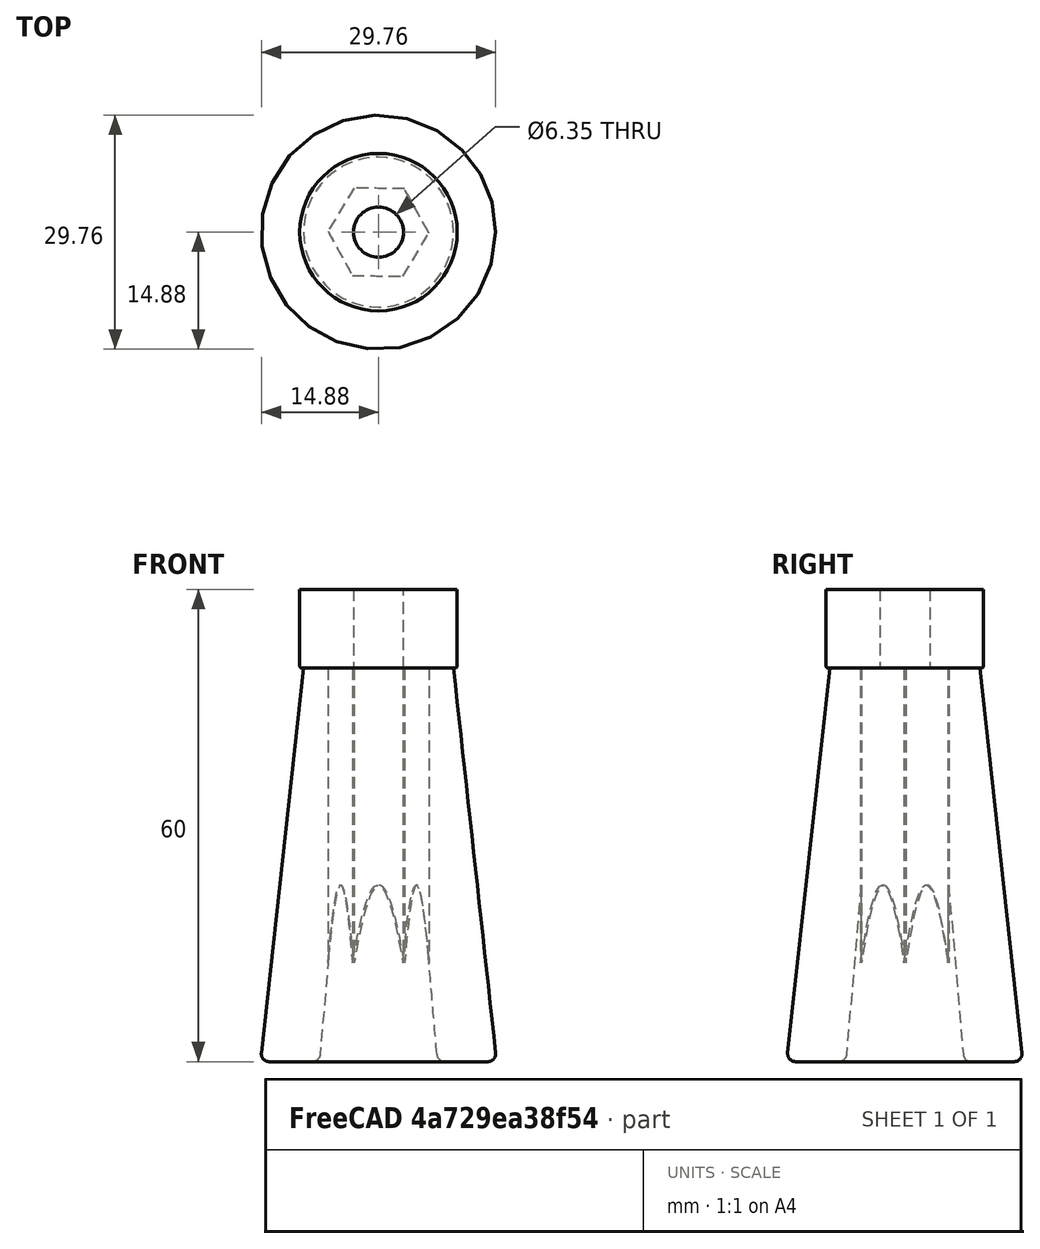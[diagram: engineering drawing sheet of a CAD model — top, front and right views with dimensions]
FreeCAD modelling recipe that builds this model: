
FCSTD DOCUMENT  (FreeCAD 0.19R24291 (Git))
Label: WorkBenchHandle_0_25x20Bolt
License: All rights reserved
LicenseURL: http://en.wikipedia.org/wiki/All_rights_reserved
objects: TechDraw::DrawViewDimension×9, Sketcher::SketchObject×5, TechDraw::DrawProjGroupItem×4, PartDesign::Pocket×2, PartDesign::Fillet×2, PartDesign::AdditiveLoft×1, PartDesign::Pad×1, TechDraw::DrawSVGTemplate×1, PartDesign::Body×1, TechDraw::DrawProjGroup×1, TechDraw::DrawPage×1
note: 18 computed .brp shape members not serialized (recipe doc carries the construction recipe); baked Part::Feature solids carry a one-line shape summary decoded from their .brp

FEATURE [Sketcher::SketchObject] Sketch
  FullyConstrained = true
  MapMode = 5
  Support = -> [XY_Plane]
  sketch-geometry (2):
    g0: Circle CenterX=0 CenterY=0 CenterZ=0 NormalX=0 NormalY=0 NormalZ=1 AngleXU=0 Radius=15
    g1: Circle CenterX=0 CenterY=0 CenterZ=0 NormalX=0 NormalY=0 NormalZ=1 AngleXU=0 Radius=7.5
  constraints (4):
    c: Coincident(g0,g-1)
    c: Coincident(g1,g0)
    c: Diameter(g0) = 30
    c: Diameter(g1) = 15
FEATURE [Sketcher::SketchObject] Sketch001
  AttachmentOffset = pos=(0,0,50) rot=(0,0,1;0rad)
  FullyConstrained = true
  MapMode = 5
  Placement = pos=(0,0,50) rot=(0,0,1;0rad)
  Support = -> [XY_Plane]
  sketch-geometry (2):
    g0: Circle CenterX=0 CenterY=0 CenterZ=0 NormalX=0 NormalY=0 NormalZ=1 AngleXU=0 Radius=9.525
    g1: Circle CenterX=0 CenterY=0 CenterZ=0 NormalX=0 NormalY=0 NormalZ=1 AngleXU=0 Radius=3.175
  constraints (4):
    c: Coincident(g0,g-1)
    c: Coincident(g1,g0)
    c: Diameter(g0) = 19.05
    c: Diameter(g1) = 6.35
FEATURE [PartDesign::AdditiveLoft] AdditiveLoft  label="AdditiveLoftHandel"
  Closed = false
  Profile = -> Sketch
  Ruled = false
  Sections = -> [Sketch001]
FEATURE [Sketcher::SketchObject] Sketch002
  FullyConstrained = true
  MapMode = 5
  Placement = pos=(0,0,50) rot=(0,0,1;0rad)
  Support = -> [AdditiveLoft]
  sketch-geometry (1):
    g0: Circle CenterX=0 CenterY=0 CenterZ=0 NormalX=0 NormalY=0 NormalZ=1 AngleXU=0 Radius=10
  constraints (2):
    c: Coincident(g0,g-1)
    c: Diameter(g0) = 20
FEATURE [PartDesign::Pad] Pad  label="PadBoss"
  BaseFeature = -> AdditiveLoft
  Direction = (1,1,1)
  Length = 10
  Length2 = 100
  Profile = -> Sketch002
  Type = 0
FEATURE [TechDraw::DrawSVGTemplate] Template
  EditableTexts = Approved1=Approved 1; Approved2=Approved 2; CheckedBy=on 20230706; Code=Code; CompanyAddress=3433 Riegeway Trail; CompanyName=Amused Scientist; DrawingNumber=Drawing Number; DrawingTitle1=WorkBenchHandle; DrawingTitle2=Drawing Title 2; DrawingTitle3=Drawing Title 3; DrawnBy=Lee Erickson; Revision=Rev; Scale=Scale 1:1; Sheet=Sheet n of m
  Height = 215.9
  Orientation = 1
  Width = 279.4
FEATURE [Sketcher::SketchObject] Sketch003
  FullyConstrained = true
  MapMode = 5
  Support = -> [XY_Plane]
  sketch-geometry (1):
    g0: Circle CenterX=0 CenterY=0 CenterZ=0 NormalX=0 NormalY=0 NormalZ=1 AngleXU=0 Radius=3.175
  constraints (2):
    c: Coincident(g0,g-1)
    c: Diameter(g0) = 6.35
FEATURE [PartDesign::Pocket] Pocket  label="PocketBoltHole"
  BaseFeature = -> Pad
  Length = 5.08
  Length2 = 100.076
  Profile = -> Sketch003
  Reversed = true
  Type = 1
FEATURE [Sketcher::SketchObject] Sketch004
  FullyConstrained = false
  MapMode = 5
  Placement = pos=(0,0,50) rot=(0,0,1;0rad)
  Support = -> [AdditiveLoft]
  sketch-geometry (7):
    g0: LineSegment StartX=6.41484 StartY=-0.111105 StartZ=0 EndX=3.30364 EndY=5.49986 EndZ=0
    g1: LineSegment StartX=3.30364 StartY=5.49986 StartZ=0 EndX=-3.1112 EndY=5.61097 EndZ=0
    g2: LineSegment StartX=-3.1112 StartY=5.61097 StartZ=0 EndX=-6.41484 EndY=0.111105 EndZ=0
    g3: LineSegment StartX=-6.41484 StartY=0.111105 StartZ=0 EndX=-3.30364 EndY=-5.49986 EndZ=0
    g4: LineSegment StartX=-3.30364 StartY=-5.49986 StartZ=0 EndX=3.1112 EndY=-5.61097 EndZ=0
    g5: LineSegment StartX=3.1112 StartY=-5.61097 StartZ=0 EndX=6.41484 EndY=-0.111105 EndZ=0
    g6: Circle CenterX=0 CenterY=0 CenterZ=0 NormalX=0 NormalY=0 NormalZ=1 AngleXU=0 Radius=6.4158
  constraints (15):
    c: Coincident(g0,g1)
    c: Coincident(g1,g2)
    c: Coincident(g2,g3)
    c: Coincident(g3,g4)
    c: Coincident(g4,g5)
    c: Coincident(g5,g0)
    c: Equal(g0, g1-g5) x5
    c: PointOnObject(g0,g6)
    c: PointOnObject(g1,g6)
    c: PointOnObject(g2,g6)
    c: PointOnObject(g3,g6)
    c: PointOnObject(g4,g6)
    c: PointOnObject(g5,g6)
    c: Coincident(g6,g-1)
    c: Distance(g1,g0) = 11.1125
FEATURE [PartDesign::Pocket] Pocket001
  BaseFeature = -> Pocket
  Length = 5.08
  Length2 = 100.076
  Profile = -> Sketch004
  Type = 1
FEATURE [PartDesign::Fillet] Fillet
  Base = -> Pocket001 [Edge2]
  BaseFeature = -> Pocket001
  Radius = 0.254
  SupportTransform = false
FEATURE [PartDesign::Fillet] Fillet001
  Base = -> Fillet [Edge18,Edge10]
  BaseFeature = -> Fillet
  Radius = 0.999998
  SupportTransform = false
FEATURE [PartDesign::Body] Body
  Group = -> [Sketch,Sketch001,AdditiveLoft,Sketch002,Pad,Sketch003,Pocket,Sketch004,Pocket001,Fillet,Fillet001]
  Origin = -> Origin
  Tip = -> Fillet001
FEATURE [TechDraw::DrawProjGroupItem] ProjItem004  label="Front001"
  CoarseView = false
  Direction = (1,0,0)
  Focus = 100
  HardHidden = false
  IsoCount = 0
  IsoHidden = false
  IsoVisible = false
  LockPosition = true
  Perspective = false
  Rotation = 0
  RotationVector = (0,0,1)
  ScaleType = 2
  SeamHidden = false
  SeamVisible = false
  SmoothHidden = false
  SmoothVisible = false
  Source = -> [Body]
  Type = 0
  X = 0
  XDirection = (0,0,1)
  Y = 0
FEATURE [TechDraw::DrawProjGroupItem] ProjItem005  label="FrontBottomLeft001"
  CoarseView = false
  Direction = (0.57735,0.57735,-0.57735)
  Focus = 100
  HardHidden = false
  IsoCount = 0
  IsoHidden = false
  IsoVisible = false
  LockPosition = true
  Perspective = false
  Rotation = 0
  RotationVector = (1,0,0)
  ScaleType = 2
  SeamHidden = false
  SeamVisible = false
  SmoothHidden = false
  SmoothVisible = false
  Source = -> [Body]
  Type = 8
  X = 90.1975
  XDirection = (0.707107,0,0.707107)
  Y = 67.4708
FEATURE [TechDraw::DrawProjGroupItem] ProjItem006  label="Right001"
  CoarseView = false
  Direction = (1e-16,0,1)
  Focus = 100
  HardHidden = false
  IsoCount = 0
  IsoHidden = false
  IsoVisible = false
  LockPosition = true
  Perspective = false
  Rotation = 0
  RotationVector = (1,0,0)
  ScaleType = 2
  SeamHidden = false
  SeamVisible = false
  SmoothHidden = false
  SmoothVisible = false
  Source = -> [Body]
  Type = 2
  X = -69.895
  XDirection = (-1,0,1e-16)
  Y = 0
FEATURE [TechDraw::DrawProjGroupItem] ProjItem007  label="FrontBottomRight001"
  CoarseView = false
  Direction = (0.57735,0.57735,0.57735)
  Focus = 100
  HardHidden = false
  IsoCount = 0
  IsoHidden = false
  IsoVisible = false
  LockPosition = true
  Perspective = false
  Rotation = 0
  RotationVector = (1,0,0)
  ScaleType = 2
  SeamHidden = false
  SeamVisible = false
  SmoothHidden = false
  SmoothVisible = false
  Source = -> [Body]
  Type = 9
  X = -5.79715
  XDirection = (-0.707107,0,0.707107)
  Y = 61.3243
FEATURE [TechDraw::DrawProjGroup] ProjGroup001  label="ProjGroup"
  Anchor = -> ProjItem004
  AutoDistribute = true
  LockPosition = false
  ProjectionType = 0
  Rotation = 0
  ScaleType = 0
  Source = -> [Body]
  Views = -> [ProjItem004,ProjItem005,ProjItem006,ProjItem007]
  X = 120.351
  Y = 96.2835
  spacingX = 15
  spacingY = 15
FEATURE [TechDraw::DrawViewDimension] Dimension010
  Arbitrary = false
  ArbitraryTolerances = false
  EqualTolerance = true
  FormatSpec = %.2f
  FormatSpecOverTolerance = %+.2f
  FormatSpecUnderTolerance = %+.2f
  Inverted = false
  LockPosition = false
  MeasureType = 1
  OverTolerance = 0
  References2D = -> [ProjItem004]
  Rotation = 0
  ScaleType = 0
  TheoreticalExact = false
  Type = 1
  UnderTolerance = 0
  X = 50.3096
  Y = 17.2342
FEATURE [TechDraw::DrawViewDimension] Dimension011
  Arbitrary = false
  ArbitraryTolerances = false
  EqualTolerance = true
  FormatSpec = %.2f
  FormatSpecOverTolerance = %+.2f
  FormatSpecUnderTolerance = %+.2f
  Inverted = false
  LockPosition = false
  MeasureType = 1
  OverTolerance = 0
  References2D = -> [ProjItem004]
  Rotation = 0
  ScaleType = 0
  TheoreticalExact = false
  Type = 2
  UnderTolerance = 0
  X = 96.2885
  Y = 6.82798
FEATURE [TechDraw::DrawViewDimension] Dimension012
  Arbitrary = false
  ArbitraryTolerances = false
  EqualTolerance = true
  FormatSpec = %.2f
  FormatSpecOverTolerance = %+.2f
  FormatSpecUnderTolerance = %+.2f
  Inverted = false
  LockPosition = false
  MeasureType = 1
  OverTolerance = 0
  References2D = -> [ProjItem004]
  Rotation = 0
  ScaleType = 0
  TheoreticalExact = false
  Type = 2
  UnderTolerance = 0
  X = 81.4148
  Y = 22.363
FEATURE [TechDraw::DrawViewDimension] Dimension013
  Arbitrary = false
  ArbitraryTolerances = false
  EqualTolerance = true
  FormatSpec = %.2f
  FormatSpecOverTolerance = %+.2f
  FormatSpecUnderTolerance = %+.2f
  Inverted = false
  LockPosition = false
  MeasureType = 1
  OverTolerance = 0
  References2D = -> [ProjItem004]
  Rotation = 0
  ScaleType = 0
  TheoreticalExact = false
  Type = 1
  UnderTolerance = 0
  X = 25.6521
  Y = -14.7617
FEATURE [TechDraw::DrawViewDimension] Dimension014
  Arbitrary = false
  ArbitraryTolerances = false
  EqualTolerance = true
  FormatSpec = %.2f
  FormatSpecOverTolerance = %+.2f
  FormatSpecUnderTolerance = %+.2f
  Inverted = false
  LockPosition = false
  MeasureType = 1
  OverTolerance = 0
  References2D = -> [ProjItem004]
  Rotation = 0
  ScaleType = 0
  TheoreticalExact = false
  Type = 1
  UnderTolerance = 0
  X = 24.4376
  Y = 21.2028
FEATURE [TechDraw::DrawViewDimension] Dimension015
  Arbitrary = false
  ArbitraryTolerances = false
  EqualTolerance = true
  FormatSpec = %.2f
  FormatSpecOverTolerance = %+.2f
  FormatSpecUnderTolerance = %+.2f
  Inverted = false
  LockPosition = false
  MeasureType = 1
  OverTolerance = 0
  References2D = -> [ProjItem004]
  Rotation = 0
  ScaleType = 0
  TheoreticalExact = false
  Type = 1
  UnderTolerance = 0
  X = -16.3725
  Y = 25.6721
FEATURE [TechDraw::DrawViewDimension] Dimension016
  Arbitrary = false
  ArbitraryTolerances = false
  EqualTolerance = true
  FormatSpec = %.2f
  FormatSpecOverTolerance = %+.2f
  FormatSpecUnderTolerance = %+.2f
  Inverted = false
  LockPosition = false
  MeasureType = 1
  OverTolerance = 0
  References2D = -> [ProjItem004]
  Rotation = 0
  ScaleType = 0
  TheoreticalExact = false
  Type = 1
  UnderTolerance = 0
  X = 16.6174
  Y = 29.4666
FEATURE [TechDraw::DrawViewDimension] Dimension017
  Arbitrary = false
  ArbitraryTolerances = false
  EqualTolerance = true
  FormatSpec = %.2f
  FormatSpecOverTolerance = %+.2f
  FormatSpecUnderTolerance = %+.2f
  Inverted = false
  LockPosition = false
  MeasureType = 1
  OverTolerance = 0
  References2D = -> [ProjItem004]
  Rotation = 0
  ScaleType = 0
  TheoreticalExact = false
  Type = 2
  UnderTolerance = 0
  X = -53.2163
  Y = 2.02701
FEATURE [TechDraw::DrawViewDimension] Dimension018
  Arbitrary = false
  ArbitraryTolerances = false
  EqualTolerance = true
  FormatSpec = ⌀%.2f
  FormatSpecOverTolerance = %+.2f
  FormatSpecUnderTolerance = %+.2f
  Inverted = false
  LockPosition = false
  MeasureType = 1
  OverTolerance = 0
  References2D = -> [ProjItem004]
  Rotation = 0
  ScaleType = 0
  TheoreticalExact = false
  Type = 5
  UnderTolerance = 0
  X = 62.6584
  Y = -16.9741
FEATURE [TechDraw::DrawPage] Page  label="PageHandel"
  KeepUpdated = true
  NextBalloonIndex = 1
  ProjectionType = 0
  Template = -> Template
  Views = -> [ProjGroup001,Dimension010,Dimension011,Dimension012,Dimension013,Dimension014,Dimension015,Dimension016,Dimension017,Dimension018]
